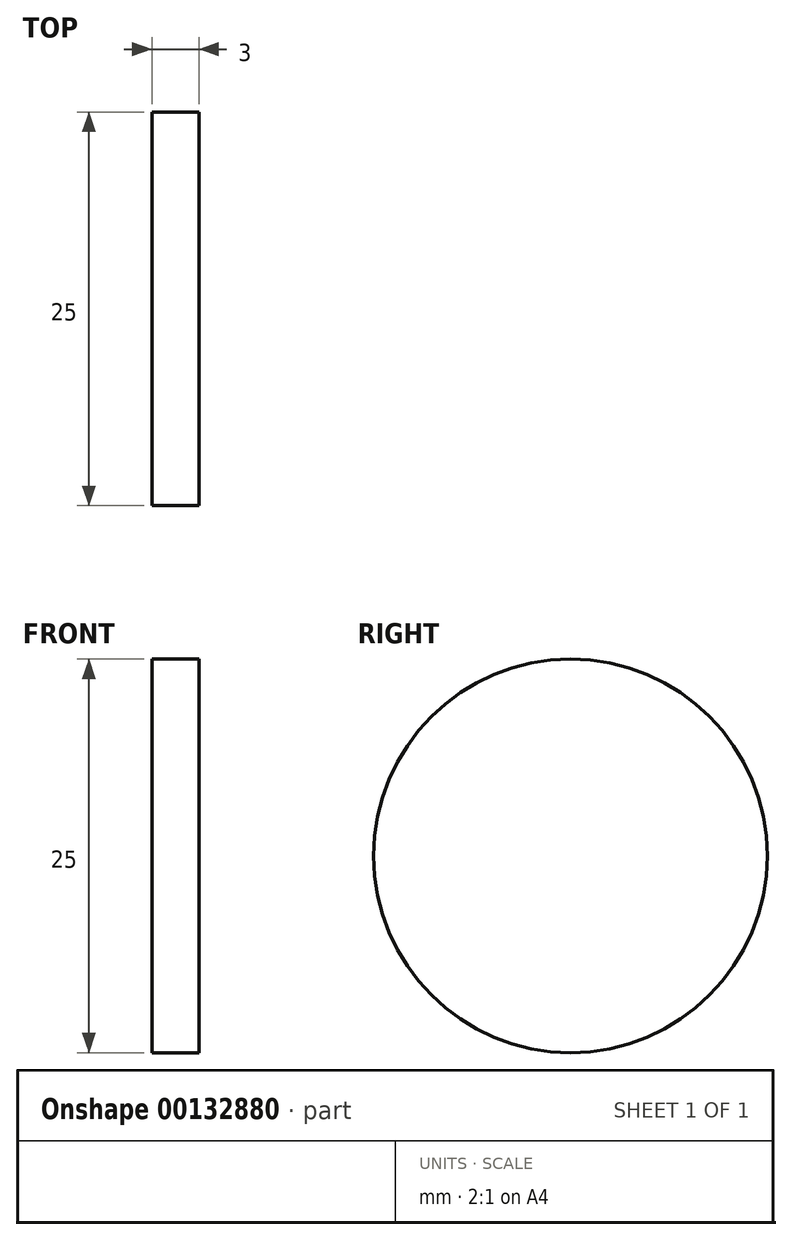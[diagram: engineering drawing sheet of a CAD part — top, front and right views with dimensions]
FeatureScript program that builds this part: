
annotation { "Feature Type Name" : "Feature", "Feature Type Description" : "" }
export const myFeature = defineFeature(function(context is Context, id is Id, definition is map)
    precondition{}
    {
        {
            var Q0;
            Q0=qCreatedBy(makeId("Right.planeOp"),FACE);
            var sketch = newSketch(context, id + "F0", { "sketchPlane" : qUnion([Q0])});
            skCircle(sketch, "E0", {"center": v(0, 0) * mm, "radius": 12.5 * mm});
            skSolve(sketch);
        }
        {
            var Q0;
            Q0 = qSketchRegion(id + "F0", true);
            extrude(context, id + "F1", {"entities" : qUnion([Q0]), "depth" : 3 * mm});
        }
    });
